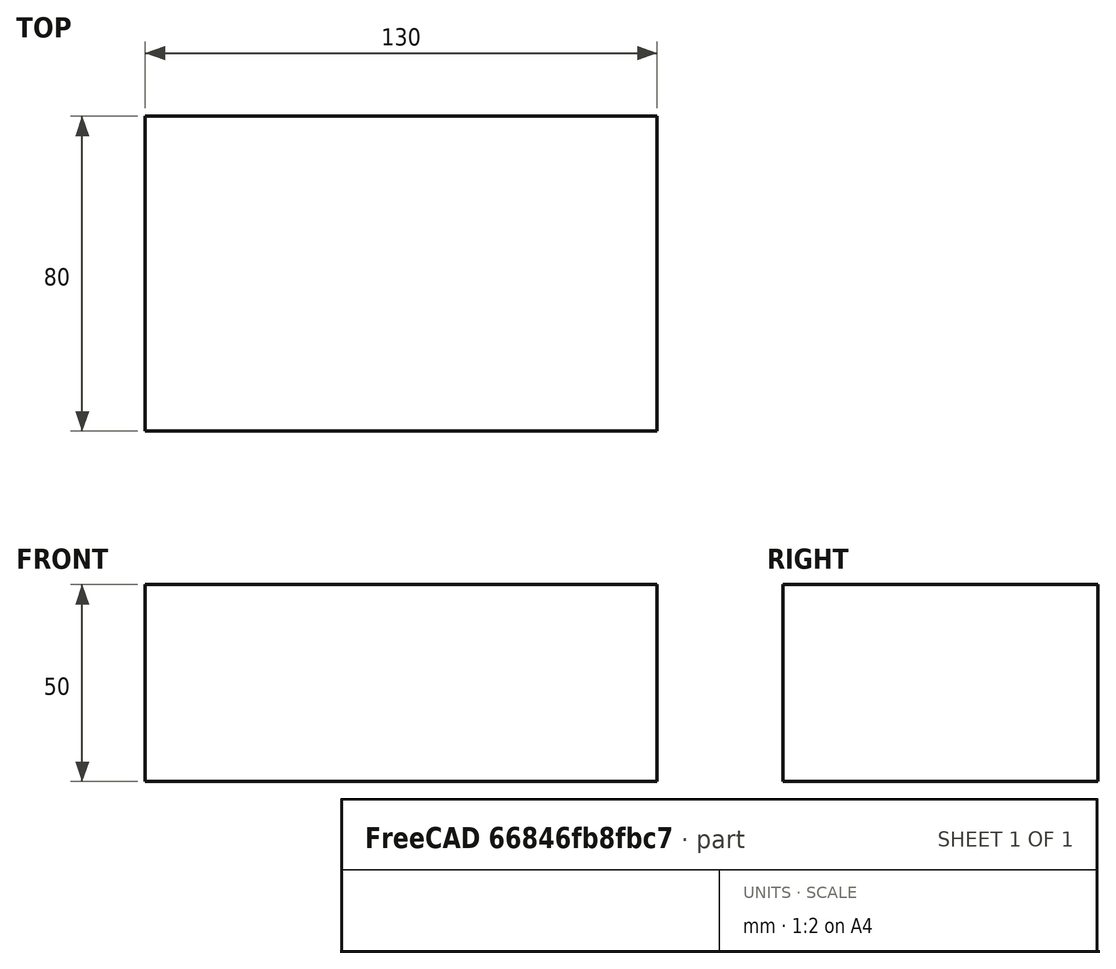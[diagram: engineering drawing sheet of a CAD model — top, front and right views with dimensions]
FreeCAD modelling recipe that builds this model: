
FCSTD DOCUMENT  (FreeCAD 0.15R4671 (Git))
Label: Flat Bar 130x80 EN10058 S235JR
License: All rights reserved
LicenseURL: http://en.wikipedia.org/wiki/All_rights_reserved
objects: Sketcher::SketchObject×1, Part::Extrusion×1
note: 2 computed .brp shape members not serialized (recipe doc carries the construction recipe); baked Part::Feature solids carry a one-line shape summary decoded from their .brp

FEATURE [Sketcher::SketchObject] Sketch
  sketch-geometry (4):
    g0: LineSegment StartX=-65 StartY=-40 StartZ=0 EndX=65 EndY=-40 EndZ=0
    g1: LineSegment StartX=65 StartY=-40 StartZ=0 EndX=65 EndY=40 EndZ=0
    g2: LineSegment StartX=65 StartY=40 StartZ=0 EndX=-65 EndY=40 EndZ=0
    g3: LineSegment StartX=-65 StartY=40 StartZ=0 EndX=-65 EndY=-40 EndZ=0
  constraints (12):
    c: Coincident(g0,g1)
    c: Coincident(g1,g2)
    c: Coincident(g2,g3)
    c: Coincident(g3,g0)
    c: Horizontal(g0)
    c: Horizontal(g2)
    c: Vertical(g1)
    c: Vertical(g3)
    c: Symmetric(g1,g2,g-2)
    c: Symmetric(g0,g1,g-1)
    c: DistanceY(g1) = 80
    c: DistanceX(g0) = 130
FEATURE [Part::Extrusion] Extrude  label="Flat Bar 130x80 EN10058 S235JR"
  Base = -> Sketch
  Dir = (0,0,50)
  Solid = true
